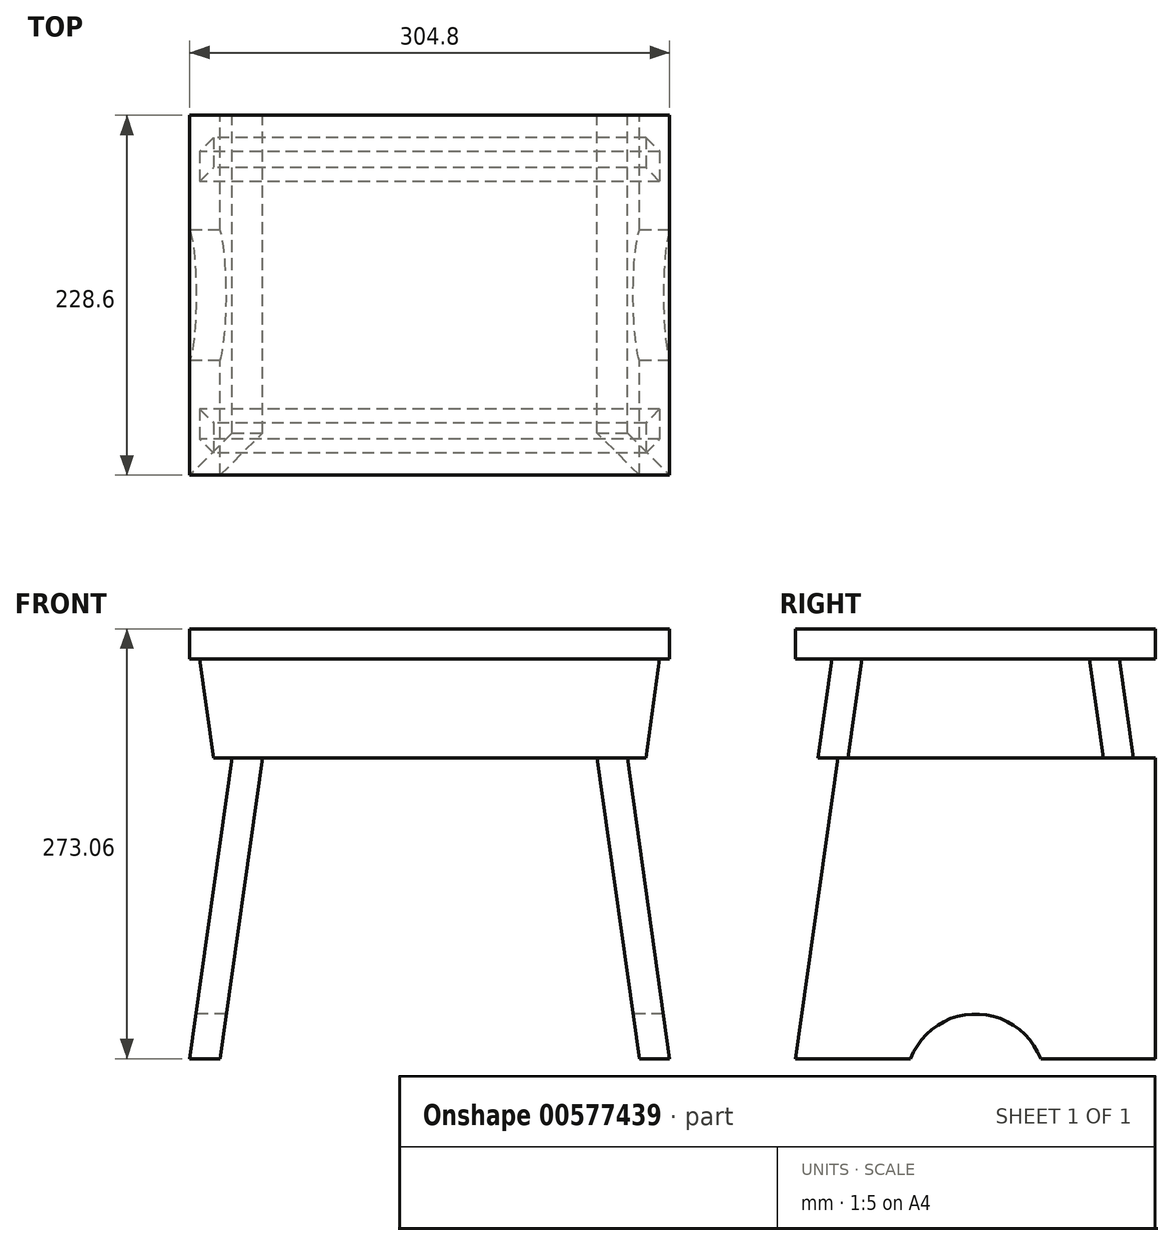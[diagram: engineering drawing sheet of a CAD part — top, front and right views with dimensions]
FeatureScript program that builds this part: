
annotation { "Feature Type Name" : "Feature", "Feature Type Description" : "" }
export const myFeature = defineFeature(function(context is Context, id is Id, definition is map)
    precondition{}
    {
        {
            var Q0;
            Q0=qCreatedBy(makeId("Front.planeOp"),FACE);
            var sketch = newSketch(context, id + "F0", { "sketchPlane" : qUnion([Q0])});
            skLineSegment(sketch, "E0.bottom", {"start": v(152.4, 9.53) * mm, "end": v(-152.4, 9.53) * mm});
            skLineSegment(sketch, "E0.top", {"start": v(152.4, -9.52) * mm, "end": v(-152.4, -9.52) * mm});
            skLineSegment(sketch, "E0.left", {"start": v(152.4, 9.53) * mm, "end": v(152.4, -9.52) * mm});
            skLineSegment(sketch, "E0.right", {"start": v(-152.4, 9.52) * mm, "end": v(-152.4, -9.52) * mm});
            skPoint(sketch, "E0.middle", {"position": v(0, 0) * mm});
            skLineSegment(sketch, "E1.bottom", {"start": v(-152.4, -9.52) * mm, "end": v(152.4, -9.52) * mm, "construction": true});
            skLineSegment(sketch, "E1.top", {"start": v(-152.4, -263.53) * mm, "end": v(152.4, -263.53) * mm, "construction": true});
            skLineSegment(sketch, "E1.left", {"start": v(-152.4, -9.52) * mm, "end": v(-152.4, -263.53) * mm, "construction": true});
            skLineSegment(sketch, "E1.right", {"start": v(152.4, -9.52) * mm, "end": v(152.4, -263.53) * mm, "construction": true});
            skLineSegment(sketch, "E2", {"start": v(116.7, -9.53) * mm, "end": v(152.4, -263.53) * mm});
            skLineSegment(sketch, "E3", {"start": v(133.16, -263.53) * mm, "end": v(97.47, -9.52) * mm});
            skLineSegment(sketch, "E4", {"start": v(0, -3.06) * mm, "end": v(0, -263.53) * mm, "construction": true});
            skLineSegment(sketch, "E5.MirrorCS", {"start": v(-133.16, -263.53) * mm, "end": v(-97.47, -9.53) * mm});
            skLineSegment(sketch, "E6.MirrorCS", {"start": v(-116.7, -9.52) * mm, "end": v(-152.4, -263.53) * mm});
            skLineSegment(sketch, "E7.bottom", {"start": v(-152.4, -9.52) * mm, "end": v(152.4, -9.52) * mm});
            skLineSegment(sketch, "E7.top", {"start": v(-152.4, -72.61) * mm, "end": v(152.4, -72.61) * mm});
            skLineSegment(sketch, "E7.left", {"start": v(-152.4, -9.52) * mm, "end": v(-152.4, -72.61) * mm});
            skLineSegment(sketch, "E7.right", {"start": v(152.4, -9.52) * mm, "end": v(152.4, -72.61) * mm});
            skLineSegment(sketch, "E8", {"start": v(146.05, -9.52) * mm, "end": v(137.18, -72.61) * mm});
            skLineSegment(sketch, "E9.MirrorCS", {"start": v(-146.05, -9.53) * mm, "end": v(-137.18, -72.61) * mm});
            skLineSegment(sketch, "E10", {"start": v(-116.7, -9.52) * mm, "end": v(-97.47, -9.52) * mm});
            skLineSegment(sketch, "E11", {"start": v(-152.4, -263.53) * mm, "end": v(-133.16, -263.53) * mm});
            skLineSegment(sketch, "E12", {"start": v(133.16, -263.53) * mm, "end": v(152.4, -263.53) * mm});
            skLineSegment(sketch, "E13", {"start": v(116.7, -9.52) * mm, "end": v(97.47, -9.52) * mm});
            skSolve(sketch);
        }
        {
            var Q0;
            Q0=makeQuery(id+"F0.imprint","IMPRINT",FACE,{"disambiguationData":[TD([[makeQuery(id+"F0.imprint","IMPRINT",EDGE,{"derivedFrom":sQuery(id+"F0.wireOp",EDGE,"E0.bottom")}),1.0]])]});
            extrude(context, id + "F1", {"entities" : qUnion([Q0]), "endBound" : BoundingType.SYMMETRIC, "depth" : 228.6 * mm, "offsetDistance" : 25.4 * mm});
        }
        {
            var Q0;
            {var subQ0=sQuery(id+"F0.wireOp",EDGE,"E10");Q0=makeQuery(id+"F0.imprint","IMPRINT",FACE,{"disambiguationData":[TD([[makeQuery(id+"F0.imprint","IMPRINT",EDGE,{"derivedFrom":subQ0}),-1.0]])]});}
            var Q1;
            {var subQ0=sQuery(id+"F0.wireOp",EDGE,"E11");Q1=makeQuery(id+"F0.imprint","IMPRINT",FACE,{"disambiguationData":[TD([[makeQuery(id+"F0.imprint","IMPRINT",EDGE,{"derivedFrom":subQ0}),1.0]])]});}
            var Q2;
            {var subQ0=sQuery(id+"F0.wireOp",EDGE,"E13");Q2=makeQuery(id+"F0.imprint","IMPRINT",FACE,{"disambiguationData":[TD([[makeQuery(id+"F0.imprint","IMPRINT",EDGE,{"derivedFrom":subQ0}),1.0]])]});}
            var Q3;
            {var subQ0=sQuery(id+"F0.wireOp",EDGE,"E12");Q3=makeQuery(id+"F0.imprint","IMPRINT",FACE,{"disambiguationData":[TD([[makeQuery(id+"F0.imprint","IMPRINT",EDGE,{"derivedFrom":subQ0}),1.0]])]});}
            var Q4;
            Q4=makeQuery(id+"F1.opExtrude","CAP_VERTEX",VERTEX,{"disambiguationData":[OSD([sQuery(id+"F0.wireOp",EDGE,"E0.left"),sQuery(id+"F0.wireOp",EDGE,"E7.bottom"),sQuery(id+"F0.wireOp",EDGE,"E7.right")])],"isStart":false});
            var Q5;
            Q5=makeQuery(id+"F1.opExtrude","CAP_VERTEX",VERTEX,{"disambiguationData":[OSD([sQuery(id+"F0.wireOp",EDGE,"E0.left"),sQuery(id+"F0.wireOp",EDGE,"E7.bottom"),sQuery(id+"F0.wireOp",EDGE,"E7.right")])],"isStart":true});
            extrude(context, id + "F2", {"entities" : qUnion([Q0, Q1, Q2, Q3]), "endBound" : BoundingType.UP_TO_VERTEX, "depth" : 25.4 * mm, "endBoundEntityVertex" : qUnion([Q4]), "offsetDistance" : 25.4 * mm, "hasSecondDirection" : true, "secondDirectionBound" : SecondDirectionBoundingType.UP_TO_VERTEX, "secondDirectionOppositeDirection" : true, "secondDirectionDepth" : 25.4 * mm, "secondDirectionBoundEntityVertex" : qUnion([Q5])});
        }
        {
            var Q0;
            Q0=qCreatedBy(makeId("Right.planeOp"),FACE);
            var sketch = newSketch(context, id + "F3", { "sketchPlane" : qUnion([Q0])});
            skLineSegment(sketch, "E14.0.0", {"start": v(114.3, -9.53) * mm, "end": v(-114.3, -9.53) * mm});
            skLineSegment(sketch, "E14.0.1", {"start": v(-114.3, -9.53) * mm, "end": v(-114.3, -263.53) * mm});
            skLineSegment(sketch, "E14.0.2", {"start": v(-114.3, -263.53) * mm, "end": v(114.3, -263.53) * mm});
            skLineSegment(sketch, "E14.0.3", {"start": v(114.3, -263.53) * mm, "end": v(114.3, -9.53) * mm});
            skLineSegment(sketch, "E15", {"start": v(-114.3, -263.53) * mm, "end": v(-78.6, -9.53) * mm});
            skLineSegment(sketch, "E16.MirrorCS", {"start": v(114.3, -9.53) * mm, "end": v(114.3, -263.53) * mm});
            skLineSegment(sketch, "E17.MirrorCS", {"start": v(114.3, -263.53) * mm, "end": v(78.6, -9.53) * mm});
            skArc(sketch, "E18", {"start": v(41.4, -263.53) * mm, "mid": v(0, -235.06) * mm, "end": v(-41.4, -263.53) * mm});
            skLineSegment(sketch, "E19", {"start": v(0, -279.42) * mm, "end": v(0, -263.53) * mm});
            skSolve(sketch);
        }
        {
            var Q0;
            {var subQ0=sQuery(id+"F3.wireOp",EDGE,"E18");Q0=makeQuery(id+"F3.imprint","IMPRINT",FACE,{"disambiguationData":[TD([[makeQuery(id+"F3.imprint","IMPRINT",EDGE,{"derivedFrom":subQ0}),1.0]])]});}
            var Q1;
            {var subQ0=sQuery(id+"F3.wireOp",EDGE,"E14.0.1");Q1=makeQuery(id+"F3.imprint","IMPRINT",FACE,{"disambiguationData":[TD([[makeQuery(id+"F3.imprint","IMPRINT",EDGE,{"derivedFrom":subQ0}),1.0]])]});}
            var Q2;
            {var subQ0=sQuery(id+"F3.wireOp",EDGE,"E16.MirrorCS");Q2=makeQuery(id+"F3.imprint","IMPRINT",FACE,{"disambiguationData":[TD([[makeQuery(id+"F3.imprint","IMPRINT",EDGE,{"derivedFrom":subQ0}),-1.0]])]});}
            extrude(context, id + "F4", {"entities" : qUnion([Q0, Q1, Q2]), "operationType" : NewBodyOperationType.REMOVE, "endBound" : BoundingType.THROUGH_ALL, "depth" : 25.4 * mm, "offsetDistance" : 25.4 * mm, "hasSecondDirection" : true, "secondDirectionBound" : SecondDirectionBoundingType.THROUGH_ALL, "secondDirectionOppositeDirection" : true, "secondDirectionDepth" : 25.4 * mm});
        }
        {
            var Q0;
            Q0=qCreatedBy(makeId("Right.planeOp"),FACE);
            var sketch = newSketch(context, id + "F5", { "sketchPlane" : qUnion([Q0])});
            skLineSegment(sketch, "E20.0", {"start": v(-114.3, -263.52) * mm, "end": v(-78.6, -9.52) * mm});
            skLineSegment(sketch, "E21.0", {"start": v(-114.3, -9.52) * mm, "end": v(114.3, -9.52) * mm});
            skLineSegment(sketch, "E22.0", {"start": v(114.3, -263.52) * mm, "end": v(78.6, -9.52) * mm});
            skLineSegment(sketch, "E23", {"start": v(-91.43, -9.52) * mm, "end": v(-100.3, -72.61) * mm});
            skLineSegment(sketch, "E24", {"start": v(-100.3, -72.61) * mm, "end": v(-81.06, -72.61) * mm});
            skLineSegment(sketch, "E25", {"start": v(-81.06, -72.61) * mm, "end": v(-72.2, -9.52) * mm});
            skLineSegment(sketch, "E26", {"start": v(-72.2, -9.52) * mm, "end": v(-91.43, -9.52) * mm});
            skLineSegment(sketch, "E27", {"start": v(-81.06, -72.61) * mm, "end": v(16.95, -72.61) * mm, "construction": true});
            skLineSegment(sketch, "E28.MirrorCS", {"start": v(81.06, -72.61) * mm, "end": v(72.2, -9.52) * mm});
            skLineSegment(sketch, "E29.MirrorCS", {"start": v(91.43, -9.52) * mm, "end": v(100.3, -72.61) * mm});
            skLineSegment(sketch, "E30.MirrorCS", {"start": v(100.3, -72.61) * mm, "end": v(81.06, -72.61) * mm});
            skLineSegment(sketch, "E31.MirrorCS", {"start": v(72.2, -9.52) * mm, "end": v(91.43, -9.52) * mm});
            skSolve(sketch);
        }
        {
            var Q0;
            {var subQ5=sQuery(id+"F5.wireOp",EDGE,"E28.MirrorCS");Q0=makeQuery(id+"F5.imprint","IMPRINT",FACE,{"disambiguationData":[TD([[makeQuery(id+"F5.imprint","IMPRINT",EDGE,{"derivedFrom":subQ5}),-1.0]])]});}
            var Q1;
            {var subQ5=sQuery(id+"F5.wireOp",EDGE,"E29.MirrorCS");Q1=makeQuery(id+"F5.imprint","IMPRINT",FACE,{"disambiguationData":[TD([[makeQuery(id+"F5.imprint","IMPRINT",EDGE,{"derivedFrom":subQ5}),-1.0]])]});}
            var Q2;
            {var subQ5=sQuery(id+"F5.wireOp",EDGE,"E23");Q2=makeQuery(id+"F5.imprint","IMPRINT",FACE,{"disambiguationData":[TD([[makeQuery(id+"F5.imprint","IMPRINT",EDGE,{"derivedFrom":subQ5}),1.0]])]});}
            var Q3;
            {var subQ5=sQuery(id+"F5.wireOp",EDGE,"E25");Q3=makeQuery(id+"F5.imprint","IMPRINT",FACE,{"disambiguationData":[TD([[makeQuery(id+"F5.imprint","IMPRINT",EDGE,{"derivedFrom":subQ5}),1.0]])]});}
            var Q4;
            Q4=makeQuery(id+"F1.opExtrude","SWEPT_FACE",FACE,{"disambiguationData":[OSD([sQuery(id+"F0.wireOp",EDGE,"E0.left")])]});
            var Q5;
            Q5=makeQuery(id+"F1.opExtrude","SWEPT_FACE",FACE,{"disambiguationData":[OSD([sQuery(id+"F0.wireOp",EDGE,"E0.right")])]});
            extrude(context, id + "F6", {"entities" : qUnion([Q0, Q1, Q2, Q3]), "endBound" : BoundingType.UP_TO_SURFACE, "depth" : 25.4 * mm, "endBoundEntityFace" : qUnion([Q4]), "offsetDistance" : 25.4 * mm, "hasSecondDirection" : true, "secondDirectionBound" : SecondDirectionBoundingType.UP_TO_SURFACE, "secondDirectionOppositeDirection" : true, "secondDirectionDepth" : 25.4 * mm, "secondDirectionBoundEntityFace" : qUnion([Q5])});
        }
        {
            var Q0;
            {var subQ0=sQuery(id+"F0.wireOp",EDGE,"E7.left");Q0=makeQuery(id+"F0.imprint","IMPRINT",FACE,{"disambiguationData":[TD([[makeQuery(id+"F0.imprint","IMPRINT",EDGE,{"derivedFrom":subQ0}),1.0]])]});}
            var Q1;
            {var subQ0=sQuery(id+"F0.wireOp",EDGE,"E7.right");Q1=makeQuery(id+"F0.imprint","IMPRINT",FACE,{"disambiguationData":[TD([[makeQuery(id+"F0.imprint","IMPRINT",EDGE,{"derivedFrom":subQ0}),-1.0]])]});}
            extrude(context, id + "F7", {"entities" : qUnion([Q0, Q1]), "operationType" : NewBodyOperationType.REMOVE, "endBound" : BoundingType.THROUGH_ALL, "oppositeDirection" : true, "depth" : 25.4 * mm, "offsetDistance" : 25.4 * mm, "hasSecondDirection" : true, "secondDirectionBound" : SecondDirectionBoundingType.THROUGH_ALL, "secondDirectionOppositeDirection" : false, "secondDirectionDepth" : 25.4 * mm});
        }
        {
            var Q0;
            Q0=makeQuery(id+"F2.opExtrude","SWEPT_BODY",BODY,{"disambiguationData":[OSD([sQuery(id+"F0.wireOp",EDGE,"E5.MirrorCS"),sQuery(id+"F0.wireOp",EDGE,"E6.MirrorCS"),sQuery(id+"F0.wireOp",EDGE,"E10"),sQuery(id+"F0.wireOp",EDGE,"E11")])]});
            var Q1;
            Q1=makeQuery(id+"F6.opExtrude","SWEPT_BODY",BODY,{"disambiguationData":[OSD([sQuery(id+"F5.wireOp",EDGE,"E23"),sQuery(id+"F5.wireOp",EDGE,"E24"),sQuery(id+"F5.wireOp",EDGE,"E25"),sQuery(id+"F5.wireOp",EDGE,"E26")])]});
            booleanBodies(context, id + "F8", {"operationType" : BooleanOperationType.SUBTRACTION, "tools" : qUnion([Q0]), "targets" : qUnion([Q1]), "keepTools" : true});
        }
        {
            var Q0;
            Q0=makeQuery(id+"F2.opExtrude","SWEPT_BODY",BODY,{"disambiguationData":[OSD([sQuery(id+"F0.wireOp",EDGE,"E5.MirrorCS"),sQuery(id+"F0.wireOp",EDGE,"E6.MirrorCS"),sQuery(id+"F0.wireOp",EDGE,"E10"),sQuery(id+"F0.wireOp",EDGE,"E11")])]});
            var Q1;
            Q1=makeQuery(id+"F6.opExtrude","SWEPT_BODY",BODY,{"disambiguationData":[OSD([sQuery(id+"F5.wireOp",EDGE,"E28.MirrorCS"),sQuery(id+"F5.wireOp",EDGE,"E29.MirrorCS"),sQuery(id+"F5.wireOp",EDGE,"E30.MirrorCS"),sQuery(id+"F5.wireOp",EDGE,"E31.MirrorCS")])]});
            booleanBodies(context, id + "F9", {"operationType" : BooleanOperationType.SUBTRACTION, "tools" : qUnion([Q0]), "targets" : qUnion([Q1]), "keepTools" : true});
        }
        {
            var Q0;
            Q0=makeQuery(id+"F2.opExtrude","SWEPT_BODY",BODY,{"disambiguationData":[OSD([sQuery(id+"F0.wireOp",EDGE,"E2"),sQuery(id+"F0.wireOp",EDGE,"E3"),sQuery(id+"F0.wireOp",EDGE,"E12"),sQuery(id+"F0.wireOp",EDGE,"E13")])]});
            var Q1;
            Q1=makeQuery(id+"F6.opExtrude","SWEPT_BODY",BODY,{"disambiguationData":[OSD([sQuery(id+"F5.wireOp",EDGE,"E28.MirrorCS"),sQuery(id+"F5.wireOp",EDGE,"E29.MirrorCS"),sQuery(id+"F5.wireOp",EDGE,"E30.MirrorCS"),sQuery(id+"F5.wireOp",EDGE,"E31.MirrorCS")])]});
            booleanBodies(context, id + "F10", {"operationType" : BooleanOperationType.SUBTRACTION, "tools" : qUnion([Q0]), "targets" : qUnion([Q1]), "keepTools" : true});
        }
        {
            var Q0;
            Q0=makeQuery(id+"F2.opExtrude","SWEPT_BODY",BODY,{"disambiguationData":[OSD([sQuery(id+"F0.wireOp",EDGE,"E2"),sQuery(id+"F0.wireOp",EDGE,"E3"),sQuery(id+"F0.wireOp",EDGE,"E12"),sQuery(id+"F0.wireOp",EDGE,"E13")])]});
            var Q1;
            Q1=makeQuery(id+"F6.opExtrude","SWEPT_BODY",BODY,{"disambiguationData":[OSD([sQuery(id+"F5.wireOp",EDGE,"E23"),sQuery(id+"F5.wireOp",EDGE,"E24"),sQuery(id+"F5.wireOp",EDGE,"E25"),sQuery(id+"F5.wireOp",EDGE,"E26")])]});
            booleanBodies(context, id + "F11", {"operationType" : BooleanOperationType.SUBTRACTION, "tools" : qUnion([Q0]), "targets" : qUnion([Q1]), "keepTools" : true});
        }
    });
